# Revit family: Legrand_Lighting_Management_SCS_Presence_Sensor_Wall
name_source: partatom
category: Dispositifs d'éclairage
units: mm (PartAtom-declared; Revit-internal decimal feet)

## family parameters
Conserver l'orientation des annotations = Oui
Cote de connecteur circulaire = Utiliser le diamètre
Couper avec des vides une fois chargée = Non
Hôte = Face
Partagée = Non
Point de calcul de pièce = Non
Type d'élément = Normal

## types (1)
- SCS Wall Sensor - PIR - IP55
    Alarm function = Non
    Collecteur de terre = Non
    Colour = White
    Constant light control = Non
    Cosses d'artère secondaire = Non
    Description = Lighting management - wall/surface mounting  - IR 180° - 6 x 15 front range
    Detection angle horizontal (MAX) (°) = 180
    Detection angle horizontal (MIN) (°) = 180
    Diameter detection range on floor (m) = 3.5
    Dim function with dimmer basic element = Non
    Elévation par défaut = 2500 mm  [stored 8.2021 ft]
    Fabricant = Legrand
    Forced switch off = Non
    Frequency (MAX) (Hz) = 0
    Frequency (MIN) (Hz) = 0
    General Conditions of Use = https://export.legrand.com
    HVAC-control = Non
    Liaison neutre = Non
    Max. duty cycle (mn) = 1000
    Max. starting current (A) = 0
    Max. switching power (W) = 0
    Max. transmission range frontally (m) = 15
    Max. transmission range sideways (m) = 3.5
    Maximum mounting height (m) = 2.5
    Min. switch-on time (s) = 30
    Model = Movement sensor
    Modèle = 048834
    Mounting method = Surface mounted (plaster)
    Nominal voltage (V) = 0
    RAL-number (akin) = 9003
    Remote operation = Non
    Response value luminosity (MAX) (lx) = 0
    Response value luminosity (MIN) (lx) = 0
    Response value luminosity adjustable = Oui
    Response value sensitivity adjustable = Non
    Substation input = Non
    Suitable for wireless transmission = Non
    Temperature (MAX) (°C) = 0
    Temperature (MIN) (°C) = 0
    URL = http://www.legrandoc.com

note: [stored X ft] marks values corroborated as IEEE doubles in the binary element streams (Revit-internal decimal feet)
